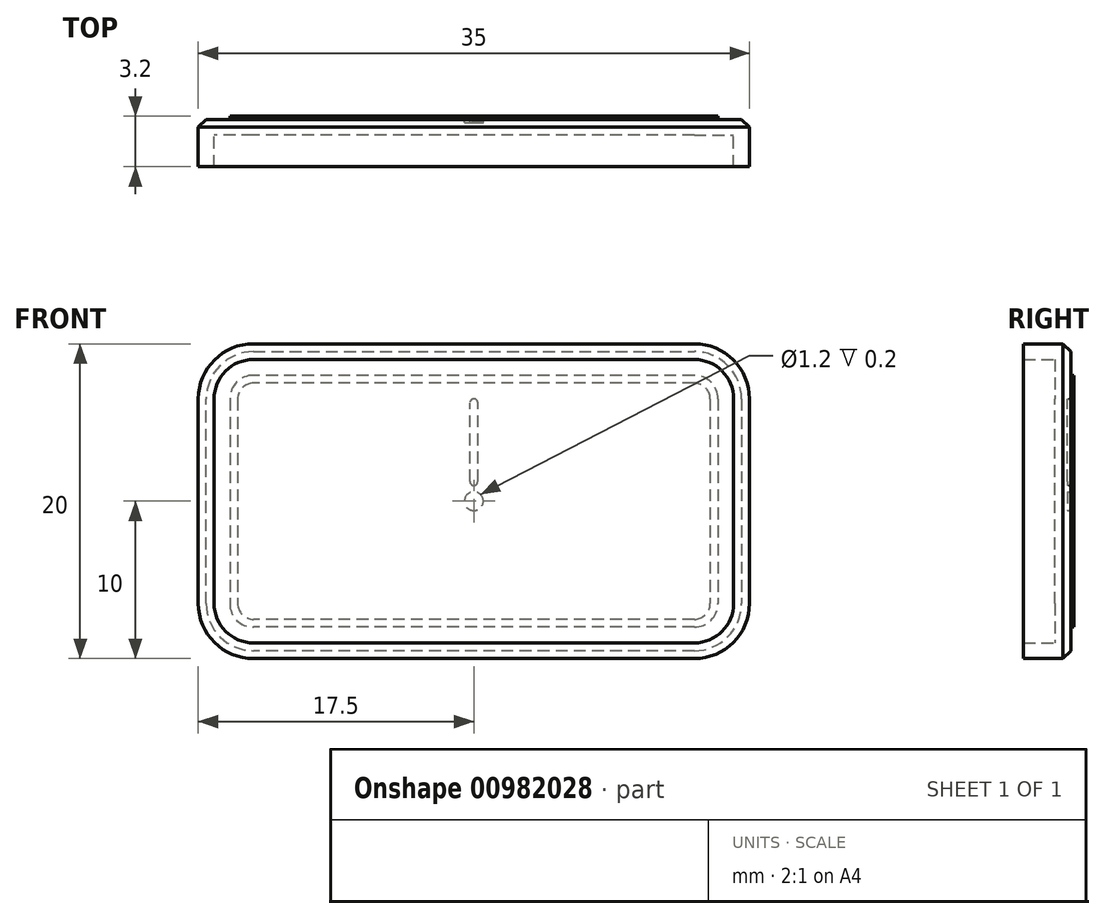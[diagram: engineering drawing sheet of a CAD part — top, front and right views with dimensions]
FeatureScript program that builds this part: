
annotation { "Feature Type Name" : "Feature", "Feature Type Description" : "" }
export const myFeature = defineFeature(function(context is Context, id is Id, definition is map)
    precondition{}
    {
        {
            var Q0;
            Q0=qCreatedBy(makeId("Front.planeOp"),FACE);
            var sketch = newSketch(context, id + "F0", { "sketchPlane" : qUnion([Q0])});
            skLineSegment(sketch, "E0.bottom", {"start": v(-17.5, 10) * mm, "end": v(17.5, 10) * mm});
            skLineSegment(sketch, "E0.top", {"start": v(-17.5, -10) * mm, "end": v(17.5, -10) * mm});
            skLineSegment(sketch, "E0.left", {"start": v(-17.5, 10) * mm, "end": v(-17.5, -10) * mm});
            skLineSegment(sketch, "E0.right", {"start": v(17.5, 10) * mm, "end": v(17.5, -10) * mm});
            skSolve(sketch);
        }
        {
            var Q0;
            Q0=makeQuery(id+"F0.imprint","IMPRINT",FACE,{"disambiguationData":[TD([[makeQuery(id+"F0.imprint","IMPRINT",EDGE,{"derivedFrom":sQuery(id+"F0.wireOp",EDGE,"E0.bottom")}),-1.0]])]});
            extrude(context, id + "F1", {"entities" : qUnion([Q0]), "depth" : 3 * mm, "offsetDistance" : 25 * mm});
        }
        {
            var Q0;
            Q0=makeQuery(id+"F1.opExtrude","SWEPT_EDGE",EDGE,{"disambiguationData":[OSD([sQuery(id+"F0.wireOp",EDGE,"E0.bottom"),sQuery(id+"F0.wireOp",EDGE,"E0.left")])]});
            var Q1;
            Q1=makeQuery(id+"F1.opExtrude","SWEPT_EDGE",EDGE,{"disambiguationData":[OSD([sQuery(id+"F0.wireOp",EDGE,"E0.bottom"),sQuery(id+"F0.wireOp",EDGE,"E0.right")])]});
            var Q2;
            Q2=makeQuery(id+"F1.opExtrude","SWEPT_EDGE",EDGE,{"disambiguationData":[OSD([sQuery(id+"F0.wireOp",EDGE,"E0.top"),sQuery(id+"F0.wireOp",EDGE,"E0.right")])]});
            var Q3;
            Q3=makeQuery(id+"F1.opExtrude","SWEPT_EDGE",EDGE,{"disambiguationData":[OSD([sQuery(id+"F0.wireOp",EDGE,"E0.top"),sQuery(id+"F0.wireOp",EDGE,"E0.left")])]});
            fillet(context, id + "F2", {"entities" : qUnion([Q0, Q1, Q2, Q3]), "tangentPropagation" : true, "radius" : 3.5 * mm, "defaultsChanged" : true, "vertexSettings" : [], "allowEdgeOverflow" : false});
        }
        {
            var Q0;
            Q0=makeQuery(id+"F1.opExtrude","CAP_FACE",FACE,{"disambiguationData":[OSD([sQuery(id+"F0.wireOp",EDGE,"E0.bottom"),sQuery(id+"F0.wireOp",EDGE,"E0.top"),sQuery(id+"F0.wireOp",EDGE,"E0.left"),sQuery(id+"F0.wireOp",EDGE,"E0.right")])],"isStart":true});
            chamfer(context, id + "F3", {"entities" : qUnion([Q0]), "width" : 0.5 * mm, "tangentPropagation" : true});
        }
        {
            var Q0;
            Q0=makeQuery(id+"F1.opExtrude","CAP_FACE",FACE,{"disambiguationData":[OSD([sQuery(id+"F0.wireOp",EDGE,"E0.bottom"),sQuery(id+"F0.wireOp",EDGE,"E0.top"),sQuery(id+"F0.wireOp",EDGE,"E0.left"),sQuery(id+"F0.wireOp",EDGE,"E0.right")])],"isStart":false});
            shell(context, id + "F4", {"entities" : qUnion([Q0]), "thickness" : 1 * mm});
        }
        {
            var Q0;
            Q0=makeQuery(id+"F1.opExtrude","CAP_FACE",FACE,{"disambiguationData":[OSD([sQuery(id+"F0.wireOp",EDGE,"E0.bottom"),sQuery(id+"F0.wireOp",EDGE,"E0.top"),sQuery(id+"F0.wireOp",EDGE,"E0.left"),sQuery(id+"F0.wireOp",EDGE,"E0.right")])],"isStart":true});
            var sketch = newSketch(context, id + "F5", { "sketchPlane" : qUnion([Q0])});
            skLineSegment(sketch, "E1.bottom", {"start": v(-15, 7.5) * mm, "end": v(15, 7.5) * mm});
            skLineSegment(sketch, "E1.top", {"start": v(-15, -7.5) * mm, "end": v(15, -7.5) * mm});
            skLineSegment(sketch, "E1.left", {"start": v(-15, 7.5) * mm, "end": v(-15, -7.5) * mm});
            skLineSegment(sketch, "E1.right", {"start": v(15, 7.5) * mm, "end": v(15, -7.5) * mm});
            skLineSegment(sketch, "E2.0", {"start": v(-15.5, 8) * mm, "end": v(-15.5, -8) * mm});
            skLineSegment(sketch, "E2.1", {"start": v(-15.5, 8) * mm, "end": v(15.5, 8) * mm});
            skLineSegment(sketch, "E2.2", {"start": v(15.5, 8) * mm, "end": v(15.5, -8) * mm});
            skLineSegment(sketch, "E2.3", {"start": v(-15.5, -8) * mm, "end": v(15.5, -8) * mm});
            skSolve(sketch);
        }
        {
            var Q0;
            Q0 = qSketchRegion(id + "F5", true);
            extrude(context, id + "F6", {"entities" : qUnion([Q0]), "operationType" : NewBodyOperationType.ADD, "depth" : 0.2 * mm, "offsetDistance" : 25 * mm});
        }
        {
            var Q0;
            Q0=makeQuery(id+"F6.opExtrude","SWEPT_EDGE",EDGE,{"disambiguationData":[OSD([sQuery(id+"F5.wireOp",EDGE,"E1.bottom"),sQuery(id+"F5.wireOp",EDGE,"E1.left")])]});
            var Q1;
            Q1=makeQuery(id+"F6.opExtrude","SWEPT_EDGE",EDGE,{"disambiguationData":[OSD([sQuery(id+"F5.wireOp",EDGE,"E1.top"),sQuery(id+"F5.wireOp",EDGE,"E1.left")])]});
            var Q2;
            Q2=makeQuery(id+"F6.opExtrude","SWEPT_EDGE",EDGE,{"disambiguationData":[OSD([sQuery(id+"F5.wireOp",EDGE,"E1.top"),sQuery(id+"F5.wireOp",EDGE,"E1.right")])]});
            var Q3;
            Q3=makeQuery(id+"F6.opExtrude","SWEPT_EDGE",EDGE,{"disambiguationData":[OSD([sQuery(id+"F5.wireOp",EDGE,"E1.bottom"),sQuery(id+"F5.wireOp",EDGE,"E1.right")])]});
            fillet(context, id + "F7", {"entities" : qUnion([Q0, Q1, Q2, Q3]), "tangentPropagation" : true, "radius" : 1 * mm, "defaultsChanged" : false, "vertexSettings" : [], "allowEdgeOverflow" : false});
        }
        {
            var Q0;
            Q0=makeQuery(id+"F6.opExtrude","SWEPT_EDGE",EDGE,{"disambiguationData":[OSD([sQuery(id+"F5.wireOp",EDGE,"E2.1"),sQuery(id+"F5.wireOp",EDGE,"E2.2")])]});
            var Q1;
            Q1=makeQuery(id+"F6.opExtrude","SWEPT_EDGE",EDGE,{"disambiguationData":[OSD([sQuery(id+"F5.wireOp",EDGE,"E2.2"),sQuery(id+"F5.wireOp",EDGE,"E2.3")])]});
            var Q2;
            Q2=makeQuery(id+"F6.opExtrude","SWEPT_EDGE",EDGE,{"disambiguationData":[OSD([sQuery(id+"F5.wireOp",EDGE,"E2.0"),sQuery(id+"F5.wireOp",EDGE,"E2.3")])]});
            var Q3;
            Q3=makeQuery(id+"F6.opExtrude","SWEPT_EDGE",EDGE,{"disambiguationData":[OSD([sQuery(id+"F5.wireOp",EDGE,"E2.0"),sQuery(id+"F5.wireOp",EDGE,"E2.1")])]});
            fillet(context, id + "F8", {"entities" : qUnion([Q0, Q1, Q2, Q3]), "tangentPropagation" : true, "radius" : 1.5 * mm, "defaultsChanged" : false, "vertexSettings" : [], "allowEdgeOverflow" : false});
        }
        {
            var Q0;
            Q0=makeQuery(id+"F6.boolean.opBoolean","SPLIT",FACE,{"disambiguationData":[TD([makeQuery(id+"F6.opExtrude","SWEPT_FACE",FACE,{"disambiguationData":[OSD([sQuery(id+"F5.wireOp",EDGE,"E1.bottom")])]})])],"derivedFrom":makeQuery(id+"F1.opExtrude","CAP_FACE",FACE,{"disambiguationData":[OSD([sQuery(id+"F0.wireOp",EDGE,"E0.bottom"),sQuery(id+"F0.wireOp",EDGE,"E0.top"),sQuery(id+"F0.wireOp",EDGE,"E0.left"),sQuery(id+"F0.wireOp",EDGE,"E0.right")])],"isStart":true})});
            var sketch = newSketch(context, id + "F9", { "sketchPlane" : qUnion([Q0])});
            skLineSegment(sketch, "E3.bottom", {"start": v(-0.25, 1) * mm, "end": v(0.25, 1) * mm});
            skLineSegment(sketch, "E3.top", {"start": v(-0.25, 6.5) * mm, "end": v(0.25, 6.5) * mm});
            skLineSegment(sketch, "E3.left", {"start": v(-0.25, 1) * mm, "end": v(-0.25, 6.5) * mm});
            skLineSegment(sketch, "E3.right", {"start": v(0.25, 1) * mm, "end": v(0.25, 6.5) * mm});
            skSolve(sketch);
        }
        {
            var Q0;
            Q0=makeQuery(id+"F9.imprint","IMPRINT",FACE,{"disambiguationData":[TD([[makeQuery(id+"F9.imprint","IMPRINT",EDGE,{"derivedFrom":sQuery(id+"F9.wireOp",EDGE,"E3.bottom")}),1.0]])]});
            extrude(context, id + "F10", {"entities" : qUnion([Q0]), "operationType" : NewBodyOperationType.REMOVE, "oppositeDirection" : true, "depth" : 0.2 * mm, "offsetDistance" : 25 * mm});
        }
        {
            var Q0;
            Q0=makeQuery(id+"F10.boolean.opBoolean","COPY",EDGE,{"derivedFrom":makeQuery(id+"F10.opExtrude","SWEPT_EDGE",EDGE,{"disambiguationData":[OSD([sQuery(id+"F9.wireOp",EDGE,"E3.bottom"),sQuery(id+"F9.wireOp",EDGE,"E3.right")])]})});
            var Q1;
            Q1=makeQuery(id+"F10.boolean.opBoolean","COPY",EDGE,{"derivedFrom":makeQuery(id+"F10.opExtrude","SWEPT_EDGE",EDGE,{"disambiguationData":[OSD([sQuery(id+"F9.wireOp",EDGE,"E3.bottom"),sQuery(id+"F9.wireOp",EDGE,"E3.left")])]})});
            var Q2;
            Q2=makeQuery(id+"F10.boolean.opBoolean","COPY",EDGE,{"derivedFrom":makeQuery(id+"F10.opExtrude","SWEPT_EDGE",EDGE,{"disambiguationData":[OSD([sQuery(id+"F9.wireOp",EDGE,"E3.top"),sQuery(id+"F9.wireOp",EDGE,"E3.right")])]})});
            var Q3;
            Q3=makeQuery(id+"F10.boolean.opBoolean","COPY",EDGE,{"derivedFrom":makeQuery(id+"F10.opExtrude","SWEPT_EDGE",EDGE,{"disambiguationData":[OSD([sQuery(id+"F9.wireOp",EDGE,"E3.top"),sQuery(id+"F9.wireOp",EDGE,"E3.left")])]})});
            fillet(context, id + "F11", {"entities" : qUnion([Q0, Q1, Q2, Q3]), "tangentPropagation" : true, "radius" : 0.25 * mm, "defaultsChanged" : false, "vertexSettings" : [], "allowEdgeOverflow" : false});
        }
        {
            var Q0;
            Q0=makeQuery(id+"F6.boolean.opBoolean","SPLIT",FACE,{"disambiguationData":[TD([makeQuery(id+"F6.opExtrude","SWEPT_FACE",FACE,{"disambiguationData":[OSD([sQuery(id+"F5.wireOp",EDGE,"E1.bottom")])]})])],"derivedFrom":makeQuery(id+"F1.opExtrude","CAP_FACE",FACE,{"disambiguationData":[OSD([sQuery(id+"F0.wireOp",EDGE,"E0.bottom"),sQuery(id+"F0.wireOp",EDGE,"E0.top"),sQuery(id+"F0.wireOp",EDGE,"E0.left"),sQuery(id+"F0.wireOp",EDGE,"E0.right")])],"isStart":true})});
            var sketch = newSketch(context, id + "F12", { "sketchPlane" : qUnion([Q0])});
            skCircle(sketch, "E4", {"center": v(0, 0) * mm, "radius": 0.6 * mm});
            skSolve(sketch);
        }
        {
            var Q0;
            Q0=makeQuery(id+"F12.imprint","IMPRINT",FACE,{"disambiguationData":[TD([[makeQuery(id+"F12.imprint","IMPRINT",EDGE,{"derivedFrom":sQuery(id+"F12.wireOp",EDGE,"E4")}),1.0]])]});
            extrude(context, id + "F13", {"entities" : qUnion([Q0]), "operationType" : NewBodyOperationType.REMOVE, "oppositeDirection" : true, "depth" : 0.2 * mm, "offsetDistance" : 25 * mm});
        }
        {
            var Q0;
            Q0=makeQuery(id+"FzVdnUFaJM4cUY4_1.1.F10.boolean.opBoolean","COPY",EDGE,{"derivedFrom":makeQuery(id+"FzVdnUFaJM4cUY4_1.1.F10.opExtrude","CAP_EDGE",EDGE,{"disambiguationData":[OSD([sQuery(id+"F9.wireOp",EDGE,"E3.left")])],"isStart":true})});
            var Q1;
            Q1=makeQuery(id+"F13.boolean.opBoolean","COPY",EDGE,{"derivedFrom":makeQuery(id+"F13.opExtrude","CAP_EDGE",EDGE,{"disambiguationData":[OSD([sQuery(id+"F12.wireOp",EDGE,"E4")])],"isStart":true})});
            var Q2;
            Q2=makeQuery(id+"F11.opFillet","BLEND_EDGE",EDGE,{"blendedFrom":[makeQuery(id+"F10.boolean.opBoolean","COPY",EDGE,{"derivedFrom":makeQuery(id+"F10.opExtrude","SWEPT_EDGE",EDGE,{"disambiguationData":[OSD([sQuery(id+"F9.wireOp",EDGE,"E3.bottom"),sQuery(id+"F9.wireOp",EDGE,"E3.left")])]})}),makeQuery(id+"F6.boolean.opBoolean","SPLIT",FACE,{"disambiguationData":[TD([makeQuery(id+"F6.opExtrude","SWEPT_FACE",FACE,{"disambiguationData":[OSD([sQuery(id+"F5.wireOp",EDGE,"E1.bottom")])]})])],"derivedFrom":makeQuery(id+"F1.opExtrude","CAP_FACE",FACE,{"disambiguationData":[OSD([sQuery(id+"F0.wireOp",EDGE,"E0.bottom"),sQuery(id+"F0.wireOp",EDGE,"E0.top"),sQuery(id+"F0.wireOp",EDGE,"E0.left"),sQuery(id+"F0.wireOp",EDGE,"E0.right")])],"isStart":true})})],"blendedInto":[makeQuery(id+"F6.boolean.opBoolean","SPLIT",FACE,{"disambiguationData":[TD([makeQuery(id+"F6.opExtrude","SWEPT_FACE",FACE,{"disambiguationData":[OSD([sQuery(id+"F5.wireOp",EDGE,"E1.bottom")])]})])],"derivedFrom":makeQuery(id+"F1.opExtrude","CAP_FACE",FACE,{"disambiguationData":[OSD([sQuery(id+"F0.wireOp",EDGE,"E0.bottom"),sQuery(id+"F0.wireOp",EDGE,"E0.top"),sQuery(id+"F0.wireOp",EDGE,"E0.left"),sQuery(id+"F0.wireOp",EDGE,"E0.right")])],"isStart":true})})]});
            fillet(context, id + "F14", {"entities" : qUnion([Q0, Q1, Q2]), "tangentPropagation" : true, "radius" : 0.1 * mm, "defaultsChanged" : false, "vertexSettings" : [], "allowEdgeOverflow" : false});
        }
    });
